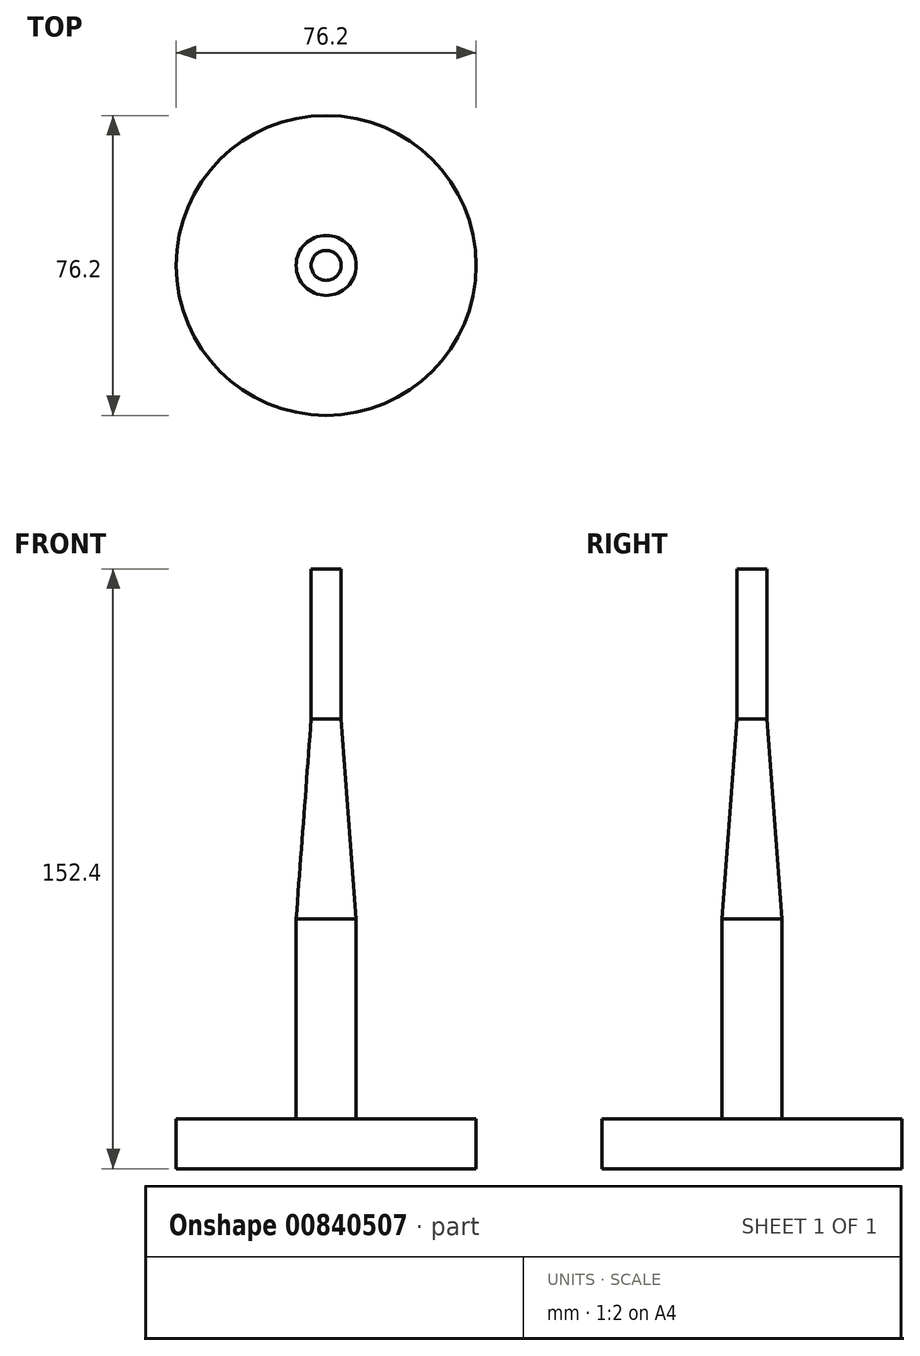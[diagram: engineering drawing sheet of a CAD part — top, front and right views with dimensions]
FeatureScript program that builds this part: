
annotation { "Feature Type Name" : "Feature", "Feature Type Description" : "" }
export const myFeature = defineFeature(function(context is Context, id is Id, definition is map)
    precondition{}
    {
        {
            var Q0;
            Q0=qCreatedBy(makeId("Top.planeOp"),FACE);
            var sketch = newSketch(context, id + "F0", { "sketchPlane" : qUnion([Q0])});
            skCircle(sketch, "E0", {"center": v(0, 0) * mm, "radius": 38.1 * mm});
            skSolve(sketch);
        }
        {
            var Q0;
            Q0=makeQuery(id+"F0.imprint","IMPRINT",FACE,{"disambiguationData":[TD([[makeQuery(id+"F0.imprint","IMPRINT",EDGE,{"derivedFrom":sQuery(id+"F0.wireOp",EDGE,"E0")}),1.0]])]});
            extrude(context, id + "F1", {"entities" : qUnion([Q0]), "depth" : 12.7 * mm, "offsetDistance" : 25.4 * mm});
        }
        {
            var Q0;
            Q0=makeQuery(id+"F1.opExtrude","CAP_FACE",FACE,{"disambiguationData":[OSD([sQuery(id+"F0.wireOp",EDGE,"E0")])],"isStart":false});
            var sketch = newSketch(context, id + "F2", { "sketchPlane" : qUnion([Q0])});
            skCircle(sketch, "E1", {"center": v(0, 0) * mm, "radius": 7.62 * mm});
            skSolve(sketch);
        }
        {
            var Q0;
            Q0=makeQuery(id+"F2.imprint","IMPRINT",FACE,{"disambiguationData":[TD([[makeQuery(id+"F2.imprint","IMPRINT",EDGE,{"derivedFrom":sQuery(id+"F2.wireOp",EDGE,"E1")}),1.0]])]});
            var Q1;
            Q1=qSketchRegion(id+"F4",true);
            extrude(context, id + "F3", {"entities" : qUnion([Q0, Q1]), "operationType" : NewBodyOperationType.ADD, "depth" : 50.8 * mm, "offsetDistance" : 25.4 * mm});
        }
        {
            var Q0;
            Q0=qCreatedBy(makeId("Right.planeOp"),FACE);
            var sketch = newSketch(context, id + "F4", { "sketchPlane" : qUnion([Q0])});
            skLineSegment(sketch, "E2", {"start": v(0, 63.5) * mm, "end": v(0, 114.3) * mm});
            skLineSegment(sketch, "E3", {"start": v(0, 114.3) * mm, "end": v(3.81, 114.3) * mm});
            skLineSegment(sketch, "E4", {"start": v(0, 63.5) * mm, "end": v(7.62, 63.5) * mm});
            skLineSegment(sketch, "E5", {"start": v(7.62, 63.5) * mm, "end": v(3.81, 114.3) * mm});
            skSolve(sketch);
        }
        {
            var Q0;
            Q0=makeQuery(id+"F4.imprint","IMPRINT",FACE,{"disambiguationData":[TD([[makeQuery(id+"F4.imprint","IMPRINT",EDGE,{"derivedFrom":sQuery(id+"F4.wireOp",EDGE,"E2")}),-1.0]])]});
            var Q1;
            Q1=sQuery(id+"F4.wireOp",EDGE,"E2");
            revolve(context, id + "F5", {"operationType" : NewBodyOperationType.ADD, "surfaceOperationType" : NewSurfaceOperationType.NEW, "entities" : qUnion([Q0]), "axis" : qUnion([Q1]), "revolveType" : RevolveType.FULL});
        }
        {
            var Q0;
            Q0=makeQuery(id+"F5.opRevolve","SWEPT_FACE",FACE,{"disambiguationData":[OSD([sQuery(id+"F4.wireOp",EDGE,"E3")])]});
            extrude(context, id + "F6", {"entities" : qUnion([Q0]), "operationType" : NewBodyOperationType.ADD, "depth" : 38.1 * mm, "offsetDistance" : 25.4 * mm});
        }
    });
